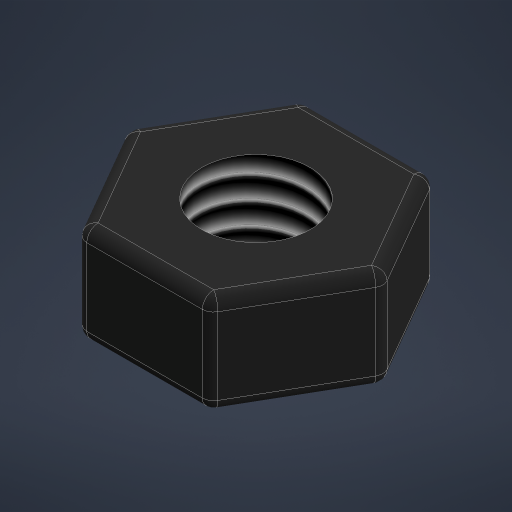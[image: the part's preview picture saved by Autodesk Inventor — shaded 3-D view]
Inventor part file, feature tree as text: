
AUTODESK INVENTOR PART (.ipt)
format: ipt  version: 2024 (Build 280153000, 153)  size: 232,960 bytes
history: native  units: mm
features: extrude x1, fillet x1, thread x1, sketch x1
ambient origin geometry x8: Origin, YZ Plane, XZ Plane, XY Plane, X Axis, Y Axis, Z Axis, Center Point
bodies: Solid1 (feature_tree)
feature tree (4):
  extrude  "Extrusion1"  Depth=0.2mm
  fillet  "Fillet1"  Radius=1.75mm
  thread  "Thread1"  [1 undecoded]
  sketch  "Sketch1"  dims[d0=3.92mm d1=1.9mm d2=1.75mm d3=0.0mm d4=0.2mm d5=2.42mm d6=0.0mm]
note: 1 required parameter value undecoded (feature->parameter linkage not recoverable at this tier; creation-order binding heuristic only, values carry confidence <= 0.55)
